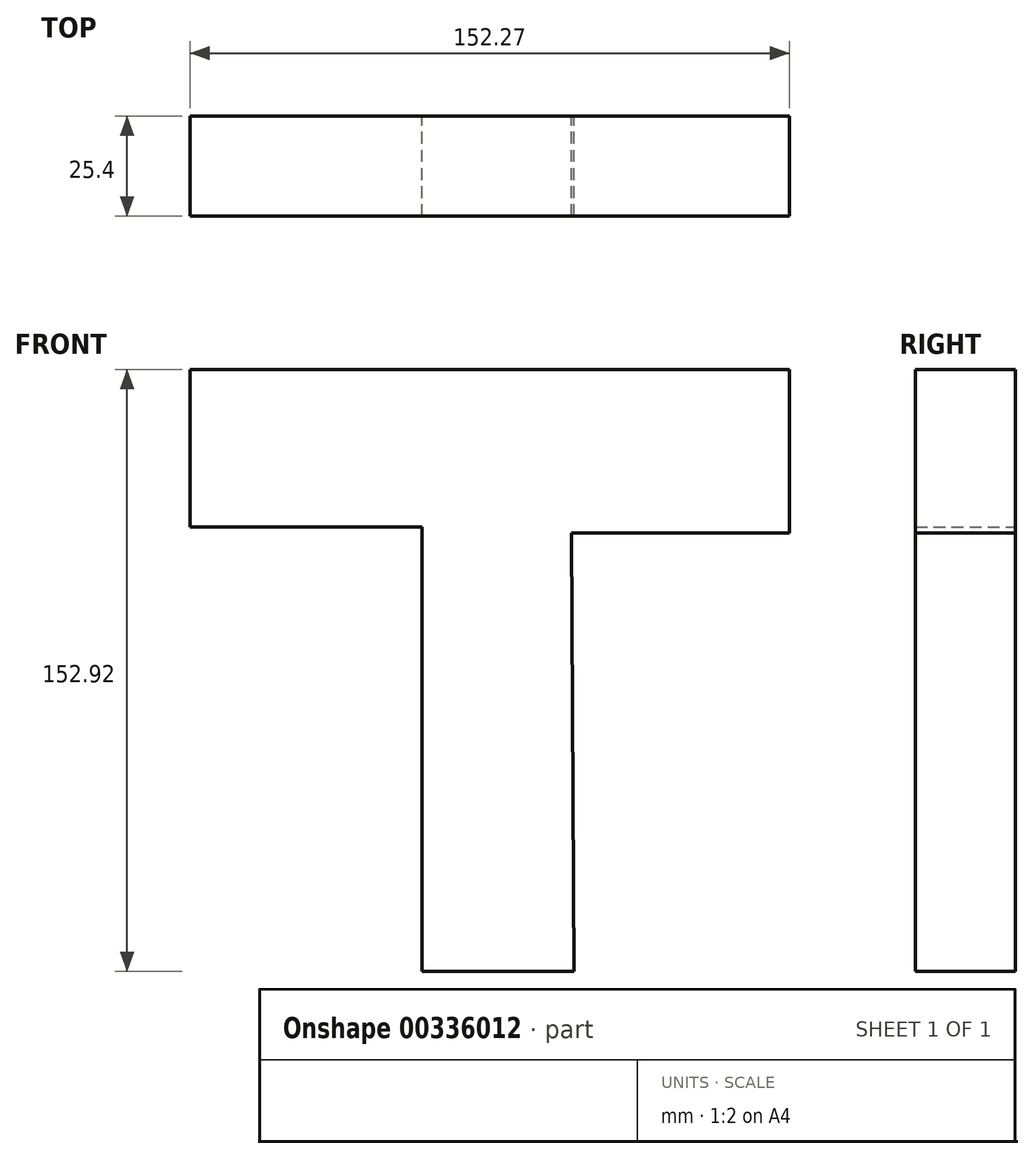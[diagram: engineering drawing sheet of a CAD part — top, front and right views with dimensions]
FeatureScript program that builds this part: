
annotation { "Feature Type Name" : "Feature", "Feature Type Description" : "" }
export const myFeature = defineFeature(function(context is Context, id is Id, definition is map)
    precondition{}
    {
        {
            var Q0;
            Q0=qCreatedBy(makeId("Front.planeOp"),FACE);
            var sketch = newSketch(context, id + "F0", { "sketchPlane" : qUnion([Q0])});
            skLineSegment(sketch, "E0", {"start": v(-75.97, 76.13) * mm, "end": v(76.3, 76.13) * mm});
            skLineSegment(sketch, "E1", {"start": v(76.3, 76.13) * mm, "end": v(76.3, 34.55) * mm});
            skLineSegment(sketch, "E2", {"start": v(-75.97, 76.13) * mm, "end": v(-75.97, 36.18) * mm});
            skLineSegment(sketch, "E3", {"start": v(76.3, 34.55) * mm, "end": v(20.96, 34.55) * mm});
            skLineSegment(sketch, "E4", {"start": v(-75.97, 36.18) * mm, "end": v(-17.03, 36.18) * mm});
            skLineSegment(sketch, "E5", {"start": v(-17.03, 36.18) * mm, "end": v(-17.03, -76.79) * mm});
            skLineSegment(sketch, "E6", {"start": v(-17.03, -76.79) * mm, "end": v(21.61, -76.79) * mm});
            skLineSegment(sketch, "E7", {"start": v(21.61, -76.79) * mm, "end": v(20.96, 34.55) * mm});
            skSolve(sketch);
        }
        {
            var Q0;
            Q0=makeQuery(id+"F0.imprint","IMPRINT",FACE,{"disambiguationData":[TD([[makeQuery(id+"F0.imprint","IMPRINT",EDGE,{"derivedFrom":sQuery(id+"F0.wireOp",EDGE,"E0")}),-1.0]])]});
            extrude(context, id + "F1", {"entities" : qUnion([Q0]), "depth" : 25.4 * mm});
        }
    });
